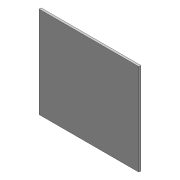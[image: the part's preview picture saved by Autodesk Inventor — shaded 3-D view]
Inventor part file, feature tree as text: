
AUTODESK INVENTOR PART (.ipt)
format: ipt  version: 2016 (Build 200138000, 138)  size: 67,072 bytes
history: native  units: mm
features: extrude x1, sketch x1
ambient origin geometry x8: Origin, YZ Plane, XZ Plane, XY Plane, X Axis, Y Axis, Z Axis, Center Point
bodies: Solid1 (feature_tree)
feature tree (2):
  extrude  "Extrusion1"  Depth=304.8mm
  sketch  "Sketch1"  dims[d0=279.4mm d1=304.8mm d2=6.35mm d3=0.0mm]
